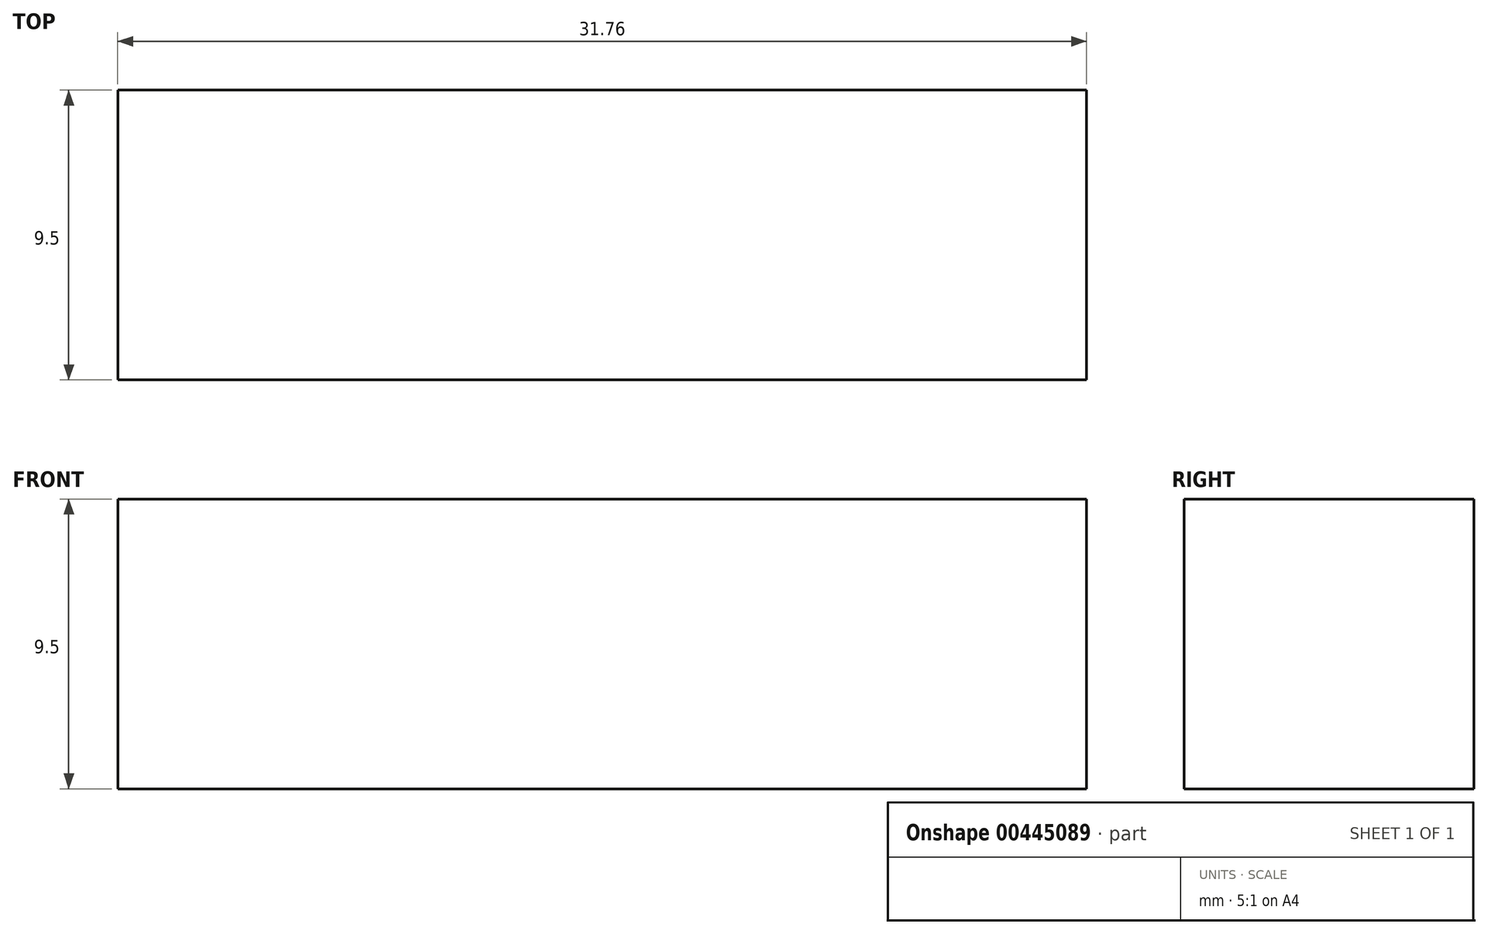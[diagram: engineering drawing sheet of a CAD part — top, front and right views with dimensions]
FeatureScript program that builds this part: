
annotation { "Feature Type Name" : "Feature", "Feature Type Description" : "" }
export const myFeature = defineFeature(function(context is Context, id is Id, definition is map)
    precondition{}
    {
        {
            var Q0;
            Q0=qCreatedBy(makeId("Front.planeOp"),FACE);
            var sketch = newSketch(context, id + "F0", { "sketchPlane" : qUnion([Q0])});
            skLineSegment(sketch, "E0.bottom", {"start": v(-15.88, 4.75) * mm, "end": v(15.88, 4.75) * mm});
            skLineSegment(sketch, "E0.top", {"start": v(-15.88, -4.75) * mm, "end": v(15.88, -4.75) * mm});
            skLineSegment(sketch, "E0.left", {"start": v(-15.88, 4.75) * mm, "end": v(-15.88, -4.75) * mm});
            skLineSegment(sketch, "E0.right", {"start": v(15.88, 4.75) * mm, "end": v(15.88, -4.75) * mm});
            skPoint(sketch, "E0.middle", {"position": v(0, 0) * mm});
            skSolve(sketch);
        }
        {
            var Q0;
            Q0 = qSketchRegion(id + "F0", true);
            extrude(context, id + "F1", {"entities" : qUnion([Q0]), "depth" : 9.5 * mm});
        }
    });
